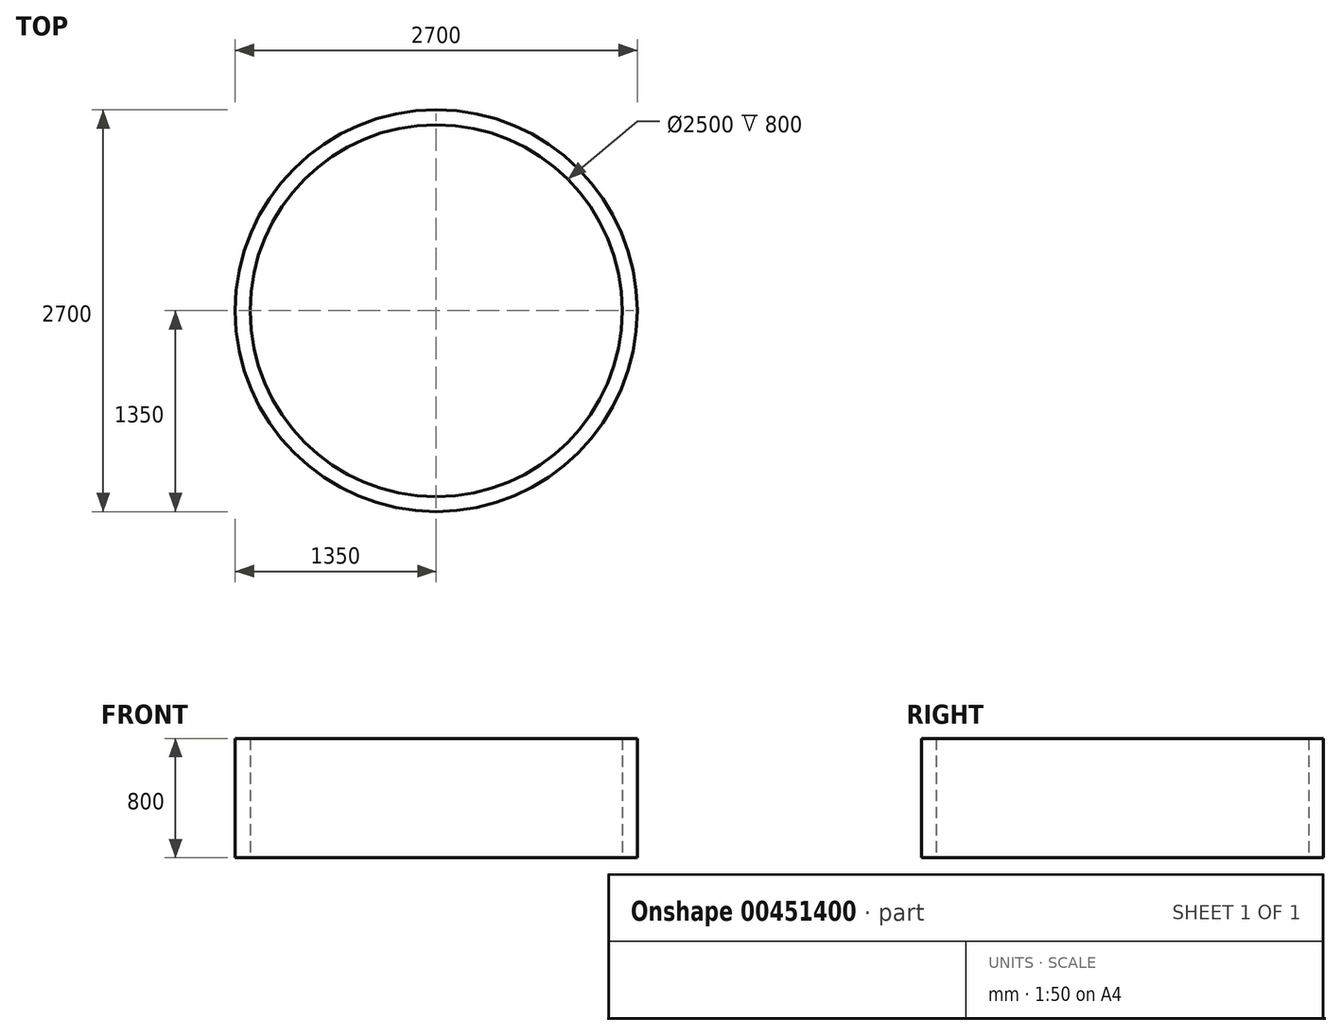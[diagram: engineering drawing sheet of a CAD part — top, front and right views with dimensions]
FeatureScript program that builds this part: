
annotation { "Feature Type Name" : "Feature", "Feature Type Description" : "" }
export const myFeature = defineFeature(function(context is Context, id is Id, definition is map)
    precondition{}
    {
        {
            var Q0;
            Q0=qCreatedBy(makeId("Top.planeOp"),FACE);
            var sketch = newSketch(context, id + "F0", { "sketchPlane" : qUnion([Q0])});
            skCircle(sketch, "E0", {"center": v(0, 0) * mm, "radius": 1350 * mm});
            skCircle(sketch, "E1", {"center": v(0, 0) * mm, "radius": 1250 * mm});
            skSolve(sketch);
        }
        {
            var Q0;
            Q0=makeQuery(id+"F0.imprint","IMPRINT",FACE,{"disambiguationData":[TD([[makeQuery(id+"F0.imprint","IMPRINT",EDGE,{"derivedFrom":sQuery(id+"F0.wireOp",EDGE,"E0")}),1.0]])]});
            extrude(context, id + "F1", {"entities" : qUnion([Q0]), "endBound" : BoundingType.SYMMETRIC, "depth" : 800 * mm});
        }
    });
